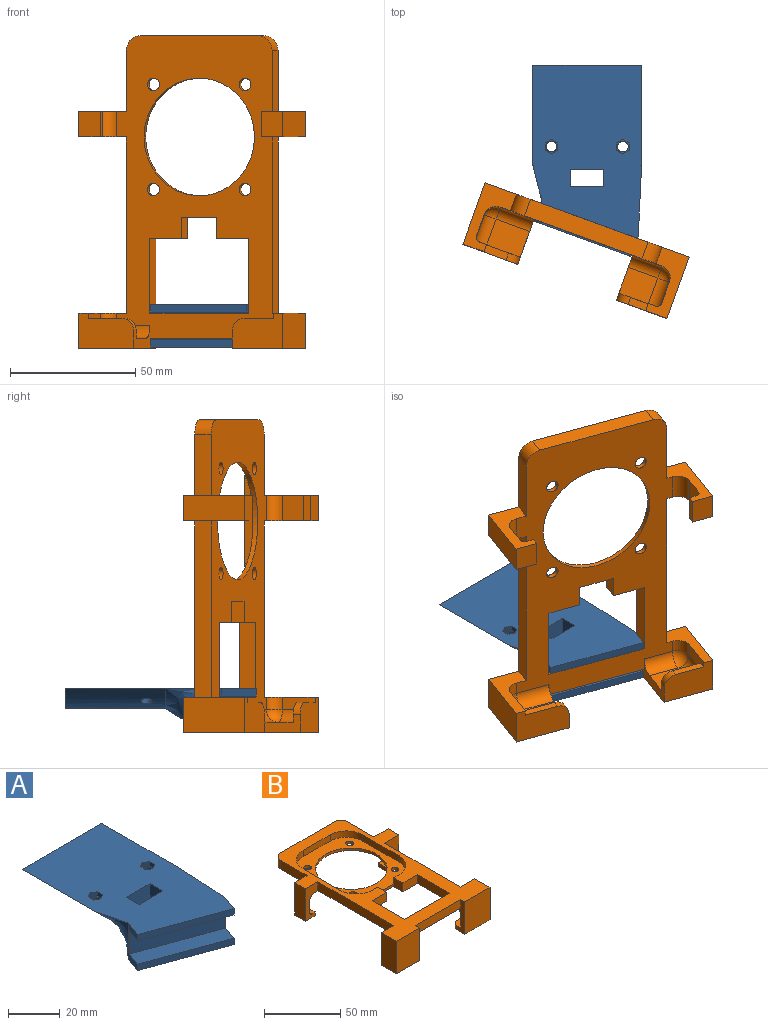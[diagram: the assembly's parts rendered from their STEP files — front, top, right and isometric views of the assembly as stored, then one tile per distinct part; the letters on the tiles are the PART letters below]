
ASSEMBLY  parts=2 mates=1
PART A: 37 faces, bbox 44.4x77.3x17.9 mm
  f0: plane 76.38x43.54mm, normal (0,0,1), area 2824.9mm2, adj f1,f3,f5,f6,f12,f13,f14,f16
  f1: bspline ~28.39x17mm, area 476.5mm2, adj f0,f2,f3,f11,f13,f34,f35
  f2: bspline ~38.53x26.9mm, area 437.4mm2, adj f1,f8,f12,f33,f34,f36
  f3: plane 17x7.99mm, normal (0.94,-0.34,0), area 62mm2, adj f0,f1,f4,f6,f7,f8,f9,f10
  f4: plane 41.09x21.07mm, normal (0,0,-1), area 307.5mm2, adj f3,f5,f6,f7
  f5: plane 17x7.99mm, normal (-0.94,0.34,0), area 62mm2, adj f0,f4,f6,f7,f8,f9,f10,f12
  f6: plane 38.53x14.02mm, normal (-0.34,-0.94,0), area 123mm2, adj f0,f3,f4,f5
  f7: plane 38.53x14.02mm, normal (-0.34,-0.94,0), area 451mm2, adj f3,f4,f5,f9
  f8: plane 41.43x22.01mm, normal (0,0,-1), area 348.5mm2, adj f2,f3,f5,f10
  f9: plane 41.09x21.07mm, normal (0,0,1), area 307.5mm2, adj f3,f5,f7,f10
  f10: plane 38.53x14.02mm, normal (-0.34,-0.94,0), area 123mm2, adj f3,f5,f8,f9
  f11: bspline ~12.99x3.18mm, area 21mm2, adj f1,f12,f15,f35
  f12: bspline ~17x16.88mm, area 257mm2, adj f0,f2,f5,f11,f14,f35,f36
  f13: cylinder r=32.5mm len=40mm, axis (0,-1,0), area 741.9mm2, adj f0,f1,f15,f16,f17
  f14: cylinder r=32.5mm len=40mm, axis (0,-1,0), area 741.9mm2, adj f0,f12,f15,f16,f18
  f15: plane 40x9.77mm, normal (0,0,-1), area 390.9mm2, adj f11,f13,f14,f16
  f16: plane 43.54x8mm, normal (0,1,0), area 247.6mm2, adj f0,f13,f14,f15
  f17: cylinder r=2.15mm len=4.3mm, axis (0,0,1), area 40.8mm2, adj f13,f25
  f18: cylinder r=2.15mm len=4.3mm, axis (0,0,1), area 40.8mm2, adj f14,f32
  f19: plane 2.5x2mm, normal (-0.5,0.87,0), area 5.8mm2, adj f0,f20,f24,f25
  f20: plane 2.89x2mm, normal (-1,0,0), area 5.8mm2, adj f0,f19,f21,f25
  f21: plane 2.5x2mm, normal (-0.5,-0.87,0), area 5.8mm2, adj f0,f20,f22,f25
  f22: plane 2.5x2mm, normal (0.5,-0.87,0), area 5.8mm2, adj f0,f21,f23,f25
  f23: plane 2.89x2mm, normal (1,0,0), area 5.8mm2, adj f0,f22,f24,f25
  f24: plane 2.5x2mm, normal (0.5,0.87,0), area 5.8mm2, adj f0,f19,f23,f25
  f25: plane 5.77x5mm, normal (0,0,1), area 7.1mm2, adj f17,f19,f20,f21,f22,f23,f24
  f26: plane 2.5x2mm, normal (-0.5,-0.87,0), area 5.8mm2, adj f0,f27,f31,f32
  f27: plane 2.5x2mm, normal (0.5,-0.87,0), area 5.8mm2, adj f0,f26,f28,f32
  f28: plane 2.89x2mm, normal (1,0,0), area 5.8mm2, adj f0,f27,f29,f32
  f29: plane 2.5x2mm, normal (0.5,0.87,0), area 5.8mm2, adj f0,f28,f30,f32
  f30: plane 2.5x2mm, normal (-0.5,0.87,0), area 5.8mm2, adj f0,f29,f31,f32
  f31: plane 2.89x2mm, normal (-1,0,0), area 5.8mm2, adj f0,f26,f30,f32
  f32: plane 5.77x5mm, normal (0,0,1), area 7.1mm2, adj f18,f26,f27,f28,f29,f30,f31
  f33: plane 13x12.49mm, normal (0,1,0), area 152.1mm2, adj f0,f2,f34,f36
  f34: plane 11.67x7.67mm, normal (-1,0,0), area 67.9mm2, adj f0,f1,f2,f33,f35
  f35: plane 13.9x9.91mm, normal (0,-1,0), area 113.1mm2, adj f0,f1,f11,f12,f34,f36
  f36: plane 12.49x7mm, normal (1,0,0), area 75.6mm2, adj f0,f2,f12,f33,f35
PART B: 79 faces, bbox 86.8x125x26 mm
  f0: plane 10x9mm, normal (-1,0,0), area 90mm2, adj f22,f24,f68,f70
  f1: plane 14x5mm, normal (1,0,0), area 61mm2, adj f34,f51,f59,f60,f66,f73
  f2: plane 14x5mm, normal (-1,0,0), area 61mm2, adj f20,f53,f57,f58,f65,f76
  f3: plane 121x68.8mm, normal (0,0,-1), area 4287.5mm2, adj f4,f5,f6,f7,f8,f9,f20,f21
  f4: plane 15x2mm, normal (0,-1,0), area 30mm2, adj f3,f10,f46,f47
  f5: cylinder r=2.5mm len=5mm, axis (0,0,-1), area 31.4mm2, adj f3,f10
  f6: cylinder r=2.5mm len=5mm, axis (0,0,-1), area 31.4mm2, adj f3,f10
  f7: cylinder r=2.5mm len=5mm, axis (0,0,-1), area 31.4mm2, adj f3,f10
  f8: cylinder r=2.5mm len=5mm, axis (0,0,-1), area 31.4mm2, adj f3,f10
  f9: cylinder r=23.5mm len=47mm, axis (0,0,-1), area 295.3mm2, adj f3,f10
  f10: plane 64x55mm, normal (0,0,1), area 1513.4mm2, adj f4,f5,f6,f7,f8,f9,f11,f12
  f11: plane 25x5mm, normal (0,-1,0), area 125mm2, adj f10,f17,f18,f49
  f12: plane 34x5mm, normal (1,0,0), area 170mm2, adj f10,f16,f17,f49
  f13: plane 5x5mm, normal (0,1,0), area 25mm2, adj f10,f16,f46,f49
  f14: plane 5x5mm, normal (0,1,0), area 25mm2, adj f10,f19,f47,f49
  f15: plane 34x5mm, normal (-1,0,0), area 170mm2, adj f10,f18,f19,f49
  f16: cylinder r=15mm len=15mm, axis (0,0,-1), area 117.8mm2, adj f10,f12,f13,f49
  f17: cylinder r=15mm len=15mm, axis (0,0,-1), area 117.8mm2, adj f10,f11,f12,f49
  f18: cylinder r=15mm len=15mm, axis (0,0,-1), area 117.8mm2, adj f10,f11,f15,f49
  f19: cylinder r=15mm len=15mm, axis (0,0,-1), area 117.8mm2, adj f10,f14,f15,f49
  f20: plane 26x13.3mm, normal (0,1,0), area 174.5mm2, adj f2,f3,f21,f48,f49,f53,f65
  f21: plane 70.5x7mm, normal (1,0,0), area 493.5mm2, adj f3,f20,f22,f49
  f22: plane 26x13.3mm, normal (0,-1,0), area 190.3mm2, adj f0,f3,f21,f23,f49,f54,f61,f62
  f23: plane 26x10mm, normal (1,0,0), area 260mm2, adj f22,f24,f49,f54
  f24: plane 26x13.3mm, normal (0,1,0), area 190.3mm2, adj f0,f3,f23,f25,f49,f54,f61,f62
  f25: plane 24.5x7mm, normal (1,0,0), area 171.5mm2, adj f3,f24,f26,f49
  f26: cylinder r=6mm len=7mm, axis (0,0,-1), area 66mm2, adj f3,f25,f27,f49
  f27: plane 50x7mm, normal (0,1,0), area 350mm2, adj f3,f26,f28,f49
  f28: cylinder r=6mm len=7mm, axis (0,0,-1), area 66mm2, adj f3,f27,f29,f49
  f29: plane 24.5x7mm, normal (-1,0,0), area 171.5mm2, adj f3,f28,f30,f49
  f30: plane 26x11.5mm, normal (0,1,0), area 177.7mm2, adj f3,f29,f31,f49,f55,f56,f63,f64
  f31: plane 26x10mm, normal (-1,0,0), area 260mm2, adj f30,f32,f49,f56
  f32: plane 26x11.5mm, normal (0,-1,0), area 177.7mm2, adj f3,f31,f33,f49,f55,f56,f63,f64
  f33: plane 70.5x7mm, normal (-1,0,0), area 493.5mm2, adj f3,f32,f34,f49
  f34: plane 26x11.5mm, normal (0,1,0), area 161.9mm2, adj f1,f3,f33,f35,f49,f51,f66
  f35: plane 26x14mm, normal (-1,0,0), area 364mm2, adj f34,f36,f49,f51
  f36: plane 26x21.5mm, normal (0,-1,0), area 559mm2, adj f35,f37,f49,f51
  f37: plane 26x9mm, normal (1,0,0), area 118.4mm2, adj f3,f36,f38,f49,f50,f51,f59,f71
  f38: plane 42x7mm, normal (0,-1,0), area 294mm2, adj f3,f37,f39,f49
  f39: plane 26x9mm, normal (-1,0,0), area 118.4mm2, adj f3,f38,f40,f49,f52,f53,f57,f74
  f40: plane 26x23.3mm, normal (0,-1,0), area 605.7mm2, adj f39,f48,f49,f53
  f41: plane 13.5x7mm, normal (0,-1,0), area 94.5mm2, adj f3,f42,f47,f49
  f42: plane 30x7mm, normal (-1,0,0), area 210mm2, adj f3,f41,f43,f49
  f43: plane 42x7mm, normal (0,1,0), area 294mm2, adj f3,f42,f44,f49
  f44: plane 30x7mm, normal (1,0,0), area 210mm2, adj f3,f43,f45,f49
  f45: plane 13.5x7mm, normal (0,-1,0), area 94.5mm2, adj f3,f44,f46,f49
  f46: plane 8.5x7mm, normal (1,0,0), area 59.5mm2, adj f3,f4,f13,f45,f49
  f47: plane 8.5x7mm, normal (-1,0,0), area 59.5mm2, adj f3,f4,f14,f41,f49
  f48: plane 26x14mm, normal (1,0,0), area 364mm2, adj f20,f40,f49,f53
  f49: plane 125x86.8mm, normal (0,0,1), area 3447.3mm2, adj f11,f12,f13,f14,f15,f16,f17,f18
  f50: plane 12.5x11mm, normal (0,1,0), area 137.5mm2, adj f37,f59,f71,f73
  f51: plane 21.5x14mm, normal (0,0,-1), area 260.6mm2, adj f1,f34,f35,f36,f37,f60,f78
  f52: plane 14.3x11mm, normal (0,1,0), area 157.3mm2, adj f39,f57,f74,f76
  f53: plane 23.3x14mm, normal (0,0,-1), area 282.2mm2, adj f2,f20,f39,f40,f48,f58,f77
  f54: plane 10x9mm, normal (0,0,-1), area 90mm2, adj f22,f23,f24,f62
  f55: plane 10x9mm, normal (1,0,0), area 90mm2, adj f30,f32,f67,f69
  f56: plane 10x9mm, normal (0,0,-1), area 90mm2, adj f30,f31,f32,f64
  f57: plane 19.3x8mm, normal (0,0,1), area 143.7mm2, adj f2,f39,f52,f58,f76,f77
  f58: plane 14.3x3mm, normal (0,1,0), area 42.9mm2, adj f2,f53,f57,f77
  f59: plane 17.5x8mm, normal (0,0,1), area 129.3mm2, adj f1,f37,f50,f60,f73,f78
  f60: plane 12.5x3mm, normal (0,1,0), area 37.5mm2, adj f1,f51,f59,f78
  f61: plane 10x3mm, normal (0,0,1), area 30mm2, adj f22,f24,f62,f70
  f62: plane 10x3mm, normal (-1,0,0), area 30mm2, adj f22,f24,f54,f61
  f63: plane 10x3mm, normal (0,0,1), area 30mm2, adj f30,f32,f64,f69
  f64: plane 10x3mm, normal (1,0,0), area 30mm2, adj f30,f32,f56,f63
  f65: cylinder r=5mm len=5mm, axis (0,-1,0), area 39.3mm2, adj f2,f3,f20,f75
  f66: cylinder r=5mm len=5mm, axis (0,1,0), area 39.3mm2, adj f1,f3,f34,f72
  f67: cylinder r=5mm len=10mm, axis (0,1,0), area 78.5mm2, adj f3,f30,f32,f55
  f68: cylinder r=5mm len=10mm, axis (0,-1,0), area 78.5mm2, adj f0,f3,f22,f24
  f69: cylinder r=2mm len=10mm, axis (0,1,0), area 31.4mm2, adj f30,f32,f55,f63
  f70: cylinder r=2mm len=10mm, axis (0,1,0), area 31.4mm2, adj f0,f22,f24,f61
  f71: cylinder r=5mm len=12.5mm, axis (-1,0,0), area 98.2mm2, adj f3,f37,f50,f72
  f72: sphere r=5mm, area 39.3mm2, adj f66,f71,f73
  f73: cylinder r=5mm len=11mm, axis (0,0,-1), area 86.4mm2, adj f1,f50,f59,f72
  f74: cylinder r=5mm len=14.3mm, axis (-1,0,0), area 112.3mm2, adj f3,f39,f52,f75
  f75: sphere r=5mm, area 39.3mm2, adj f65,f74,f76
  f76: cylinder r=5mm len=11mm, axis (0,0,-1), area 86.4mm2, adj f2,f52,f57,f75
  f77: cylinder r=5mm len=5mm, axis (0,0,-1), area 23.6mm2, adj f39,f53,f57,f58
  f78: cylinder r=5mm len=5mm, axis (0,0,-1), area 23.6mm2, adj f37,f51,f59,f60
PLACE A at identity
PLACE B rot(axis=(0.12,0.7,0.7),165.9deg) t=(-1.57,-43.9,42.87)mm
MATE fastened B.f49 <-> A.f7  axis (0.34,0.94,0) through (0.82,-37.32,-32.63)mm
